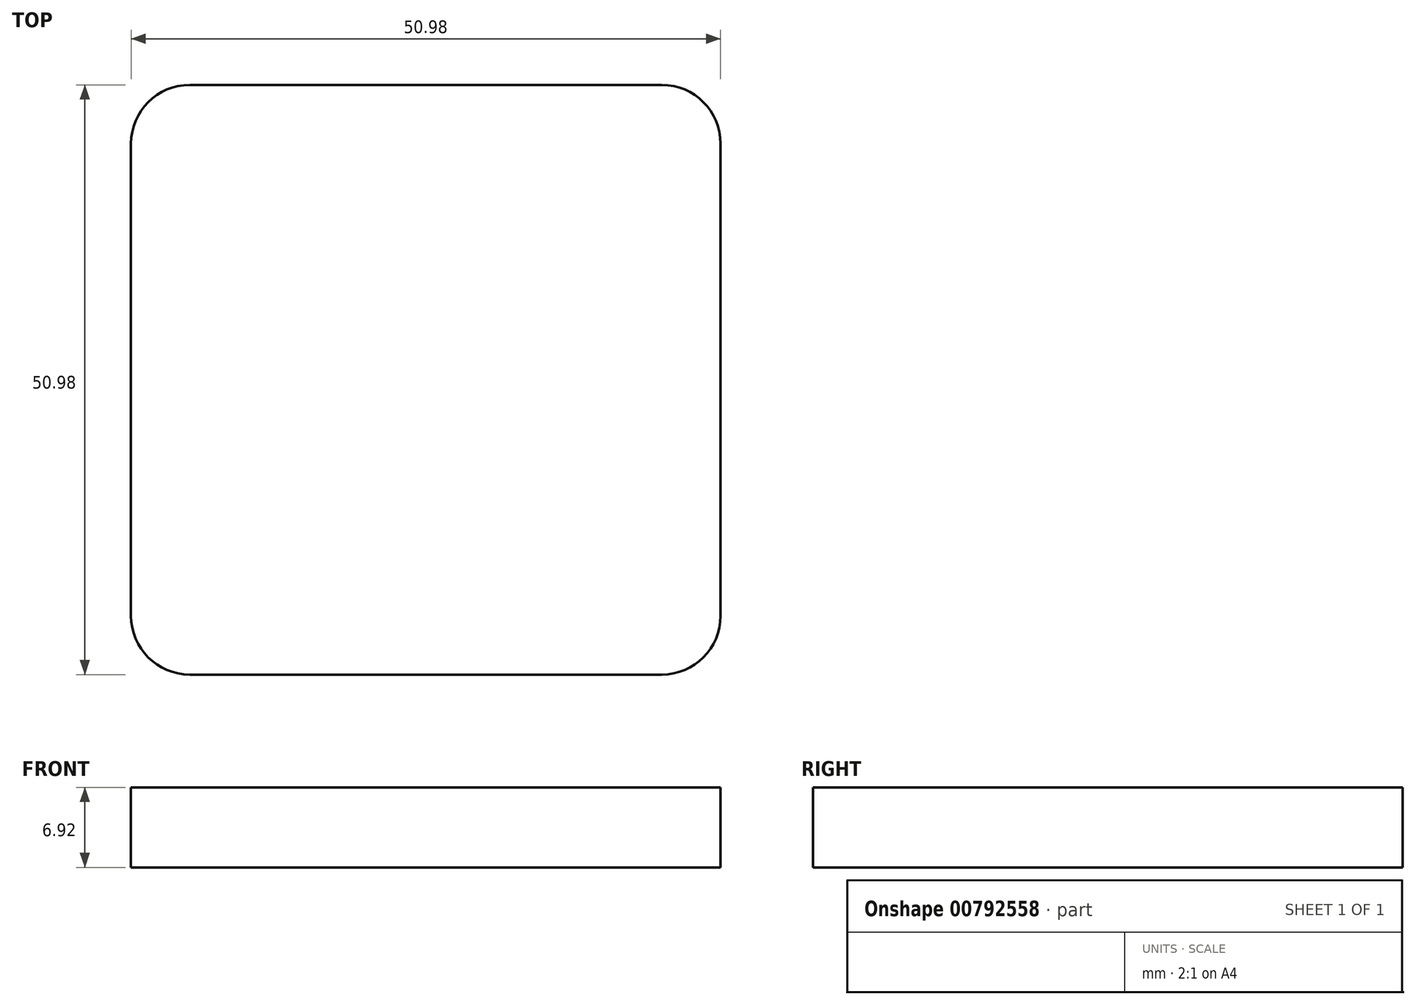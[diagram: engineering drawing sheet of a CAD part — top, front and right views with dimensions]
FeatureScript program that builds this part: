
annotation { "Feature Type Name" : "Feature", "Feature Type Description" : "" }
export const myFeature = defineFeature(function(context is Context, id is Id, definition is map)
    precondition{}
    {
        {
            var Q0;
            Q0=qCreatedBy(makeId("Top.planeOp"),FACE);
            var sketch = newSketch(context, id + "F0", { "sketchPlane" : qUnion([Q0])});
            skLineSegment(sketch, "E0.bottom", {"start": v(25.5, -25.5) * mm, "end": v(-25.5, -25.5) * mm});
            skLineSegment(sketch, "E0.top", {"start": v(25.5, 25.5) * mm, "end": v(-25.5, 25.5) * mm});
            skLineSegment(sketch, "E0.left", {"start": v(25.5, -25.5) * mm, "end": v(25.5, 25.5) * mm});
            skLineSegment(sketch, "E0.right", {"start": v(-25.5, -25.5) * mm, "end": v(-25.5, 25.5) * mm});
            skPoint(sketch, "E0.middle", {"position": v(0, 0) * mm});
            skSolve(sketch);
        }
        {
            var Q0;
            Q0=makeQuery(id+"F0.imprint","IMPRINT",FACE,{"disambiguationData":[TD([[makeQuery(id+"F0.imprint","IMPRINT",EDGE,{"derivedFrom":sQuery(id+"F0.wireOp",EDGE,"E0.bottom")}),-1.0]])]});
            extrude(context, id + "F1", {"entities" : qUnion([Q0]), "depth" : 6.92 * mm, "offsetDistance" : 25.4 * mm});
        }
        {
            var Q0;
            Q0=makeQuery(id+"F1.opExtrude","SWEPT_EDGE",EDGE,{"disambiguationData":[OSD([sQuery(id+"F0.wireOp",EDGE,"E0.bottom"),sQuery(id+"F0.wireOp",EDGE,"E0.right")])]});
            var Q1;
            Q1=makeQuery(id+"F1.opExtrude","SWEPT_EDGE",EDGE,{"disambiguationData":[OSD([sQuery(id+"F0.wireOp",EDGE,"E0.top"),sQuery(id+"F0.wireOp",EDGE,"E0.right")])]});
            var Q2;
            Q2=makeQuery(id+"F1.opExtrude","SWEPT_EDGE",EDGE,{"disambiguationData":[OSD([sQuery(id+"F0.wireOp",EDGE,"E0.top"),sQuery(id+"F0.wireOp",EDGE,"E0.left")])]});
            var Q3;
            Q3=makeQuery(id+"F1.opExtrude","SWEPT_EDGE",EDGE,{"disambiguationData":[OSD([sQuery(id+"F0.wireOp",EDGE,"E0.bottom"),sQuery(id+"F0.wireOp",EDGE,"E0.left")])]});
            fillet(context, id + "F2", {"entities" : qUnion([Q0, Q1, Q2, Q3]), "radius" : 5.08 * mm, "tangentPropagation" : true, "allowEdgeOverflow" : false});
        }
    });
